# Revit family: Casement_28_B_Side_Hung_Standard
name_source: partatom
category: Windows
revit_build: Autodesk Revit 2014 (Build: 20130308_1515(x64)
units: mm (PartAtom-declared; Revit-internal decimal feet)

## types (18) — shared parameters
Aluminium Thickness = 1 mm  [stored 0.00328084 ft]
Bead SG Gap = 13 mm  [stored 0.0426509 ft]
Casement Dimension = 28 mm  [stored 0.0918635 ft]
Custom Sash Width = 554 mm  [stored 1.81759 ft]
Default Sill Height = 800 mm  [stored 2.62467 ft]
Depth Bead = 14 mm  [stored 0.0459318 ft]
Description = Window 28mm, Type B side hung
Frame Center Offset = 14 mm  [stored 0.0459318 ft]
Limit Fixed Panel Width Max = 1500 mm
Limit Fixed Panel Width Min = 200 mm  [stored 0.656168 ft]
Limit Sash Height Max = 1200 mm
Limit Sash Height Min = 300 mm  [stored 0.984252 ft]
Limit Sash Width Max = 600 mm  [stored 1.9685 ft]
Limit Sash Width Min = 300 mm  [stored 0.984252 ft]
Limit Window Height Max = 1246 mm  [stored 4.08793 ft]
Limit Window Height Min = 346 mm
Limit Window Width Max = 2129 mm
Limit Window Width Min = 829 mm  [stored 2.71982 ft]
Manufacturer = Crealco
Model = Casement 28
Offset Bead SG Center Reversed = 14 mm  [stored 0.0459318 ft]
Offset Mullion Left = 569 mm  [stored 1.8668 ft]
Offset Panel 4 Left = 599 mm  [stored 1.96522 ft]
Offset Sash Left = 23 mm  [stored 0.0754593 ft]
Offset Sash Top = 23 mm  [stored 0.0754593 ft]
Offset Window Exterior = 14 mm  [stored 0.0459318 ft]
SG Gasket Thickness = 6 mm  [stored 0.019685 ft]
Sash Center Offset = 11 mm  [stored 0.0360892 ft]
Sash Overlap = 7 mm  [stored 0.0229659 ft]
Sash Spacing Inner = 8 mm  [stored 0.0262467 ft]
Single Glazing = Yes
URL = http://www.crealco.co.za
Wall Closure = By host
Width Bead = 15 mm  [stored 0.0492126 ft]
Width Panel 1 = 539 mm  [stored 1.76837 ft]
Width Profile = 30 mm  [stored 0.0984252 ft]
Width Sash = 524 mm  [stored 1.71916 ft]
Width Sash Opening = 554 mm  [stored 1.81759 ft]
zero-valued in all types: Window Exterior Offset

## per-type parameters (varying)
| type | Area Pane Left | Area Pane Right | Clearvue SHGC Value | Clearvue U Value | Custom Windload | Custom Window Height | Custom Window Width | Depth Mullion | Energy Advantage SHGC Value | Energy Advantage U Value | Height | Height Panel 4 | Height Sash | Height Sash Opening | Intruderprufe LowE SHGC Value | Intruderprufe LowE U Value | Intruderprufe SHGC Value | Intruderprufe U Value | Length Mullion | Max Pane Area | Mullion Depth Windload Based | Width | Width Panel 4 | Windload Design |
| 28-0909S-1000Pa | 0.37 m² | 0.21 m² | 0.577 | 6.15 | 1000 mm  [stored 3.28084 ft] | 890 mm  [stored 2.91995 ft] | 890 mm  [stored 2.91995 ft] | 29 mm  [stored 0.0951444 ft] | 0.514 | 4.75 | 890 mm  [stored 2.91995 ft] | 830 mm  [stored 2.7231 ft] | 814 mm  [stored 2.6706 ft] | 844 mm  [stored 2.76903 ft] | 0.512 | 4.54 | 0.582 | 6.13 | 890 mm  [stored 2.91995 ft] | 0.37 m² | 29 mm  [stored 0.0951444 ft] | 890 mm  [stored 2.91995 ft] | 261 mm  [stored 0.856299 ft] | 1000 mm  [stored 3.28084 ft] |
| 28-1209S-1000Pa | 0.37 m² | 0.45 m² | 0.624 | 6.1 | 1000 mm  [stored 3.28084 ft] | 890 mm  [stored 2.91995 ft] | 1190 mm  [stored 3.9042 ft] | 29 mm  [stored 0.0951444 ft] | 0.559 | 4.16 | 890 mm  [stored 2.91995 ft] | 830 mm  [stored 2.7231 ft] | 814 mm  [stored 2.6706 ft] | 844 mm  [stored 2.76903 ft] | 0.544 | 4.39 | 0.601 | 6.06 | 890 mm  [stored 2.91995 ft] | 0.45 m² | 29 mm  [stored 0.0951444 ft] | 1190 mm  [stored 3.9042 ft] | 561 mm | 1000 mm  [stored 3.28084 ft] |
| 28-1509S-1000Pa | 0.37 m² | 0.7 m² | 0.653 | 6.07 | 1000 mm  [stored 3.28084 ft] | 890 mm  [stored 2.91995 ft] | 1490 mm  [stored 4.88845 ft] | 29 mm  [stored 0.0951444 ft] | 0.58 | 4.51 | 890 mm  [stored 2.91995 ft] | 830 mm  [stored 2.7231 ft] | 814 mm  [stored 2.6706 ft] | 844 mm  [stored 2.76903 ft] | 0.563 | 4.3 | 0.625 | 6.01 | 890 mm  [stored 2.91995 ft] | 0.7 m² | 29 mm  [stored 0.0951444 ft] | 1490 mm  [stored 4.88845 ft] | 861 mm  [stored 2.8248 ft] | 1000 mm  [stored 3.28084 ft] |
| 28-0912S-1000Pa | 0.52 m² | 0.28 m² | 0.599 | 6.13 | 1000 mm  [stored 3.28084 ft] | 1190 mm  [stored 3.9042 ft] | 890 mm  [stored 2.91995 ft] | 29 mm  [stored 0.0951444 ft] | 0.541 | 4.69 | 1190 mm  [stored 3.9042 ft] | 1130 mm  [stored 3.70735 ft] | 1114 mm  [stored 3.65486 ft] | 1144 mm | 0.524 | 4.5 | 0.582 | 6.11 | 1190 mm  [stored 3.9042 ft] | 0.52 m² | 29 mm  [stored 0.0951444 ft] | 890 mm  [stored 2.91995 ft] | 261 mm  [stored 0.856299 ft] | 1000 mm  [stored 3.28084 ft] |
| 28-0912S-1500Pa | 0.52 m² | 0.28 m² | 0.599 | 6.25 | 1500 mm | 1190 mm  [stored 3.9042 ft] | 890 mm  [stored 2.91995 ft] | 54 mm  [stored 0.177165 ft] | 0.541 | 4.83 | 1190 mm  [stored 3.9042 ft] | 1130 mm  [stored 3.70735 ft] | 1114 mm  [stored 3.65486 ft] | 1144 mm | 0.524 | 4.64 | 0.564 | 6.15 | 1190 mm  [stored 3.9042 ft] | 0.52 m² | 54 mm  [stored 0.177165 ft] | 890 mm  [stored 2.91995 ft] | 261 mm  [stored 0.856299 ft] | 1500 mm |
| 28-1212S-1000Pa | 0.52 m² | 0.62 m² | 0.646 | 6.17 | 1000 mm  [stored 3.28084 ft] | 1190 mm  [stored 3.9042 ft] | 1190 mm  [stored 3.9042 ft] | 54 mm  [stored 0.177165 ft] | 0.578 | 4.63 | 1190 mm  [stored 3.9042 ft] | 1130 mm  [stored 3.70735 ft] | 1114 mm  [stored 3.65486 ft] | 1144 mm | 0.557 | 4.44 | 0.609 | 6.06 | 1190 mm  [stored 3.9042 ft] | 0.62 m² | 54 mm  [stored 0.177165 ft] | 1190 mm  [stored 3.9042 ft] | 561 mm | 1000 mm  [stored 3.28084 ft] |
| 28-1512S-1000Pa | 0.52 m² | 0.95 m² | 0.675 | 6.12 | 1000 mm  [stored 3.28084 ft] | 1190 mm  [stored 3.9042 ft] | 1490 mm  [stored 4.88845 ft] | 54 mm  [stored 0.177165 ft] | 0.6 | 4.5 | 1190 mm  [stored 3.9042 ft] | 1130 mm  [stored 3.70735 ft] | 1114 mm  [stored 3.65486 ft] | 1144 mm | 0.577 | 4.33 | 0.635 | 6.01 | 1190 mm  [stored 3.9042 ft] | 0.95 m² | 54 mm  [stored 0.177165 ft] | 1490 mm  [stored 4.88845 ft] | 861 mm  [stored 2.8248 ft] | 1000 mm  [stored 3.28084 ft] |
| 28-0909S-1500Pa | 0.37 m² | 0.21 m² | 0.577 | 6.15 | 1500 mm | 890 mm  [stored 2.91995 ft] | 890 mm  [stored 2.91995 ft] | 29 mm  [stored 0.0951444 ft] | 0.514 | 4.75 | 890 mm  [stored 2.91995 ft] | 830 mm  [stored 2.7231 ft] | 814 mm  [stored 2.6706 ft] | 844 mm  [stored 2.76903 ft] | 0.512 | 4.54 | 0.582 | 6.13 | 890 mm  [stored 2.91995 ft] | 0.37 m² | 29 mm  [stored 0.0951444 ft] | 890 mm  [stored 2.91995 ft] | 261 mm  [stored 0.856299 ft] | 1500 mm |
| 28-0909S-2000Pa | 0.37 m² | 0.21 m² | 0.577 | 6.15 | 2000 mm | 890 mm  [stored 2.91995 ft] | 890 mm  [stored 2.91995 ft] | 29 mm  [stored 0.0951444 ft] | 0.514 | 4.75 | 890 mm  [stored 2.91995 ft] | 830 mm  [stored 2.7231 ft] | 814 mm  [stored 2.6706 ft] | 844 mm  [stored 2.76903 ft] | 0.512 | 4.54 | 0.582 | 6.13 | 890 mm  [stored 2.91995 ft] | 0.37 m² | 29 mm  [stored 0.0951444 ft] | 890 mm  [stored 2.91995 ft] | 261 mm  [stored 0.856299 ft] | 2000 mm |
| 28-0912S-2000Pa | 0.52 m² | 0.28 m² | 0.599 | 6.25 | 2000 mm | 1190 mm  [stored 3.9042 ft] | 890 mm  [stored 2.91995 ft] | 54 mm  [stored 0.177165 ft] | 0.541 | 4.83 | 1190 mm  [stored 3.9042 ft] | 1130 mm  [stored 3.70735 ft] | 1114 mm  [stored 3.65486 ft] | 1144 mm | 0.524 | 4.64 | 0.564 | 6.15 | 1190 mm  [stored 3.9042 ft] | 0.52 m² | 54 mm  [stored 0.177165 ft] | 890 mm  [stored 2.91995 ft] | 261 mm  [stored 0.856299 ft] | 2000 mm |
| 28-1209S-1500Pa | 0.37 m² | 0.45 m² | 0.624 | 6.1 | 1500 mm | 890 mm  [stored 2.91995 ft] | 1190 mm  [stored 3.9042 ft] | 29 mm  [stored 0.0951444 ft] | 0.559 | 4.16 | 890 mm  [stored 2.91995 ft] | 830 mm  [stored 2.7231 ft] | 814 mm  [stored 2.6706 ft] | 844 mm  [stored 2.76903 ft] | 0.544 | 4.39 | 0.601 | 6.06 | 890 mm  [stored 2.91995 ft] | 0.45 m² | 29 mm  [stored 0.0951444 ft] | 1190 mm  [stored 3.9042 ft] | 561 mm | 1500 mm |
| 28-1209S-2000Pa | 0.37 m² | 0.45 m² | 0.624 | 6.1 | 2000 mm | 890 mm  [stored 2.91995 ft] | 1190 mm  [stored 3.9042 ft] | 29 mm  [stored 0.0951444 ft] | 0.559 | 4.16 | 890 mm  [stored 2.91995 ft] | 830 mm  [stored 2.7231 ft] | 814 mm  [stored 2.6706 ft] | 844 mm  [stored 2.76903 ft] | 0.544 | 4.39 | 0.601 | 6.06 | 890 mm  [stored 2.91995 ft] | 0.45 m² | 29 mm  [stored 0.0951444 ft] | 1190 mm  [stored 3.9042 ft] | 561 mm | 2000 mm |
| 28-1212S-1500Pa | 0.52 m² | 0.62 m² | 0.646 | 6.17 | 1500 mm | 1190 mm  [stored 3.9042 ft] | 1190 mm  [stored 3.9042 ft] | 54 mm  [stored 0.177165 ft] | 0.578 | 4.63 | 1190 mm  [stored 3.9042 ft] | 1130 mm  [stored 3.70735 ft] | 1114 mm  [stored 3.65486 ft] | 1144 mm | 0.557 | 4.44 | 0.609 | 6.06 | 1190 mm  [stored 3.9042 ft] | 0.62 m² | 54 mm  [stored 0.177165 ft] | 1190 mm  [stored 3.9042 ft] | 561 mm | 1500 mm |
| 28-1212S-2000Pa | 0.52 m² | 0.62 m² | 0.646 | 6.17 | 2000 mm | 1190 mm  [stored 3.9042 ft] | 1190 mm  [stored 3.9042 ft] | 54 mm  [stored 0.177165 ft] | 0.578 | 4.63 | 1190 mm  [stored 3.9042 ft] | 1130 mm  [stored 3.70735 ft] | 1114 mm  [stored 3.65486 ft] | 1144 mm | 0.557 | 4.44 | 0.609 | 6.06 | 1190 mm  [stored 3.9042 ft] | 0.62 m² | 54 mm  [stored 0.177165 ft] | 1190 mm  [stored 3.9042 ft] | 561 mm | 2000 mm |
| 28-1509S-1500Pa | 0.37 m² | 0.7 m² | 0.653 | 6.07 | 1500 mm | 890 mm  [stored 2.91995 ft] | 1490 mm  [stored 4.88845 ft] | 29 mm  [stored 0.0951444 ft] | 0.58 | 4.51 | 890 mm  [stored 2.91995 ft] | 830 mm  [stored 2.7231 ft] | 814 mm  [stored 2.6706 ft] | 844 mm  [stored 2.76903 ft] | 0.563 | 4.3 | 0.625 | 6.01 | 890 mm  [stored 2.91995 ft] | 0.7 m² | 29 mm  [stored 0.0951444 ft] | 1490 mm  [stored 4.88845 ft] | 861 mm  [stored 2.8248 ft] | 1500 mm |
| 28-1509S-2000Pa | 0.37 m² | 0.7 m² | 0.653 | 6.07 | 2000 mm | 890 mm  [stored 2.91995 ft] | 1490 mm  [stored 4.88845 ft] | 29 mm  [stored 0.0951444 ft] | 0.58 | 4.51 | 890 mm  [stored 2.91995 ft] | 830 mm  [stored 2.7231 ft] | 814 mm  [stored 2.6706 ft] | 844 mm  [stored 2.76903 ft] | 0.563 | 4.3 | 0.625 | 6.01 | 890 mm  [stored 2.91995 ft] | 0.7 m² | 29 mm  [stored 0.0951444 ft] | 1490 mm  [stored 4.88845 ft] | 861 mm  [stored 2.8248 ft] | 2000 mm |
| 28-1512S-1500Pa | 0.52 m² | 0.95 m² | 0.675 | 6.12 | 1500 mm | 1190 mm  [stored 3.9042 ft] | 1490 mm  [stored 4.88845 ft] | 54 mm  [stored 0.177165 ft] | 0.6 | 4.5 | 1190 mm  [stored 3.9042 ft] | 1130 mm  [stored 3.70735 ft] | 1114 mm  [stored 3.65486 ft] | 1144 mm | 0.577 | 4.33 | 0.635 | 6.01 | 1190 mm  [stored 3.9042 ft] | 0.95 m² | 54 mm  [stored 0.177165 ft] | 1490 mm  [stored 4.88845 ft] | 861 mm  [stored 2.8248 ft] | 1500 mm |
| 28-1512S-2000Pa | 0.52 m² | 0.95 m² | 0.675 | 6.12 | 2000 mm | 1190 mm  [stored 3.9042 ft] | 1490 mm  [stored 4.88845 ft] | 54 mm  [stored 0.177165 ft] | 0.6 | 4.5 | 1190 mm  [stored 3.9042 ft] | 1130 mm  [stored 3.70735 ft] | 1114 mm  [stored 3.65486 ft] | 1144 mm | 0.577 | 4.33 | 0.635 | 6.01 | 1190 mm  [stored 3.9042 ft] | 0.95 m² | 54 mm  [stored 0.177165 ft] | 1490 mm  [stored 4.88845 ft] | 861 mm  [stored 2.8248 ft] | 2000 mm |

note: [stored X ft] marks values corroborated as IEEE doubles in the binary element streams (Revit-internal decimal feet)

## geometry (parser evidence)
native form markers: Sweep x26
no freeform markers — native parametric forms only
